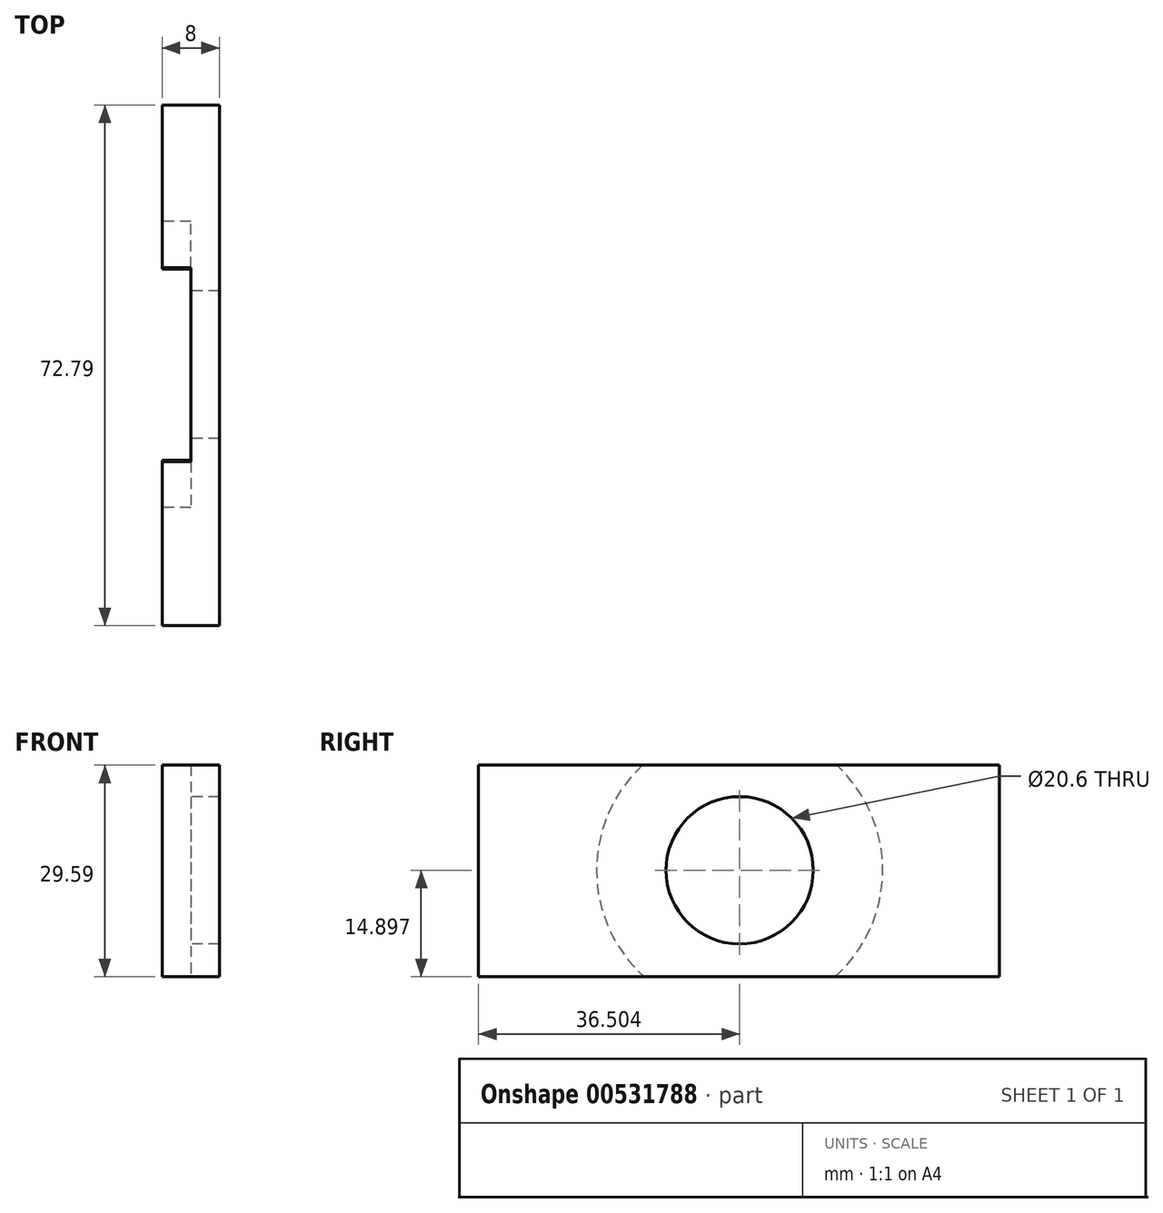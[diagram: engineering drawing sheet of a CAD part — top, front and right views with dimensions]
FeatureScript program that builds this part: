
annotation { "Feature Type Name" : "Feature", "Feature Type Description" : "" }
export const myFeature = defineFeature(function(context is Context, id is Id, definition is map)
    precondition{}
    {
        {
            var Q0;
            Q0=qCreatedBy(makeId("Right.planeOp"),FACE);
            var sketch = newSketch(context, id + "F0", { "sketchPlane" : qUnion([Q0])});
            skLineSegment(sketch, "E0.bottom", {"start": v(0, 0) * mm, "end": v(-53.74, 0) * mm});
            skLineSegment(sketch, "E0.top", {"start": v(0, -29.6) * mm, "end": v(-53.74, -29.6) * mm});
            skLineSegment(sketch, "E0.left", {"start": v(0, 0) * mm, "end": v(0, -29.6) * mm});
            skLineSegment(sketch, "E0.right", {"start": v(-53.74, 0) * mm, "end": v(-53.74, -29.6) * mm});
            skCircle(sketch, "E1", {"center": v(-23.59, -14.7) * mm, "radius": 10.3 * mm});
            skSolve(sketch);
        }
        {
            var Q0;
            Q0 = qSketchRegion(id + "F0", true);
            extrude(context, id + "F1", {"entities" : qUnion([Q0]), "depth" : 8 * mm, "offsetDistance" : 25.4 * mm});
        }
        {
            var Q0;
            Q0=makeQuery(id+"F1.opExtrude","CAP_FACE",FACE,{"disambiguationData":[OSD([sQuery(id+"F0.wireOp",EDGE,"E0.bottom"),sQuery(id+"F0.wireOp",EDGE,"E0.top"),sQuery(id+"F0.wireOp",EDGE,"E0.left"),sQuery(id+"F0.wireOp",EDGE,"E0.right"),sQuery(id+"F0.wireOp",EDGE,"E1")])],"isStart":true});
            var sketch = newSketch(context, id + "F2", { "sketchPlane" : qUnion([Q0])});
            skCircle(sketch, "E2", {"center": v(23.59, -14.7) * mm, "radius": 20 * mm});
            skSolve(sketch);
        }
        {
            var Q0;
            Q0 = qSketchRegion(id + "F2", true);
            extrude(context, id + "F3", {"entities" : qUnion([Q0]), "operationType" : NewBodyOperationType.REMOVE, "oppositeDirection" : true, "depth" : 4 * mm, "offsetDistance" : 25.4 * mm});
        }
        {
            var Q0;
            Q0=makeQuery(id+"F1.opExtrude","SWEPT_FACE",FACE,{"disambiguationData":[OSD([sQuery(id+"F0.wireOp",EDGE,"E0.left")])]});
            extrude(context, id + "F4", {"entities" : qUnion([Q0]), "operationType" : NewBodyOperationType.ADD, "depth" : 12.7 * mm, "offsetDistance" : 25.4 * mm});
        }
        {
            var Q0;
            Q0=makeQuery(id+"F1.opExtrude","SWEPT_FACE",FACE,{"disambiguationData":[OSD([sQuery(id+"F0.wireOp",EDGE,"E0.right")])]});
            extrude(context, id + "F5", {"entities" : qUnion([Q0]), "operationType" : NewBodyOperationType.ADD, "depth" : 6.35 * mm, "offsetDistance" : 25.4 * mm});
        }
    });
